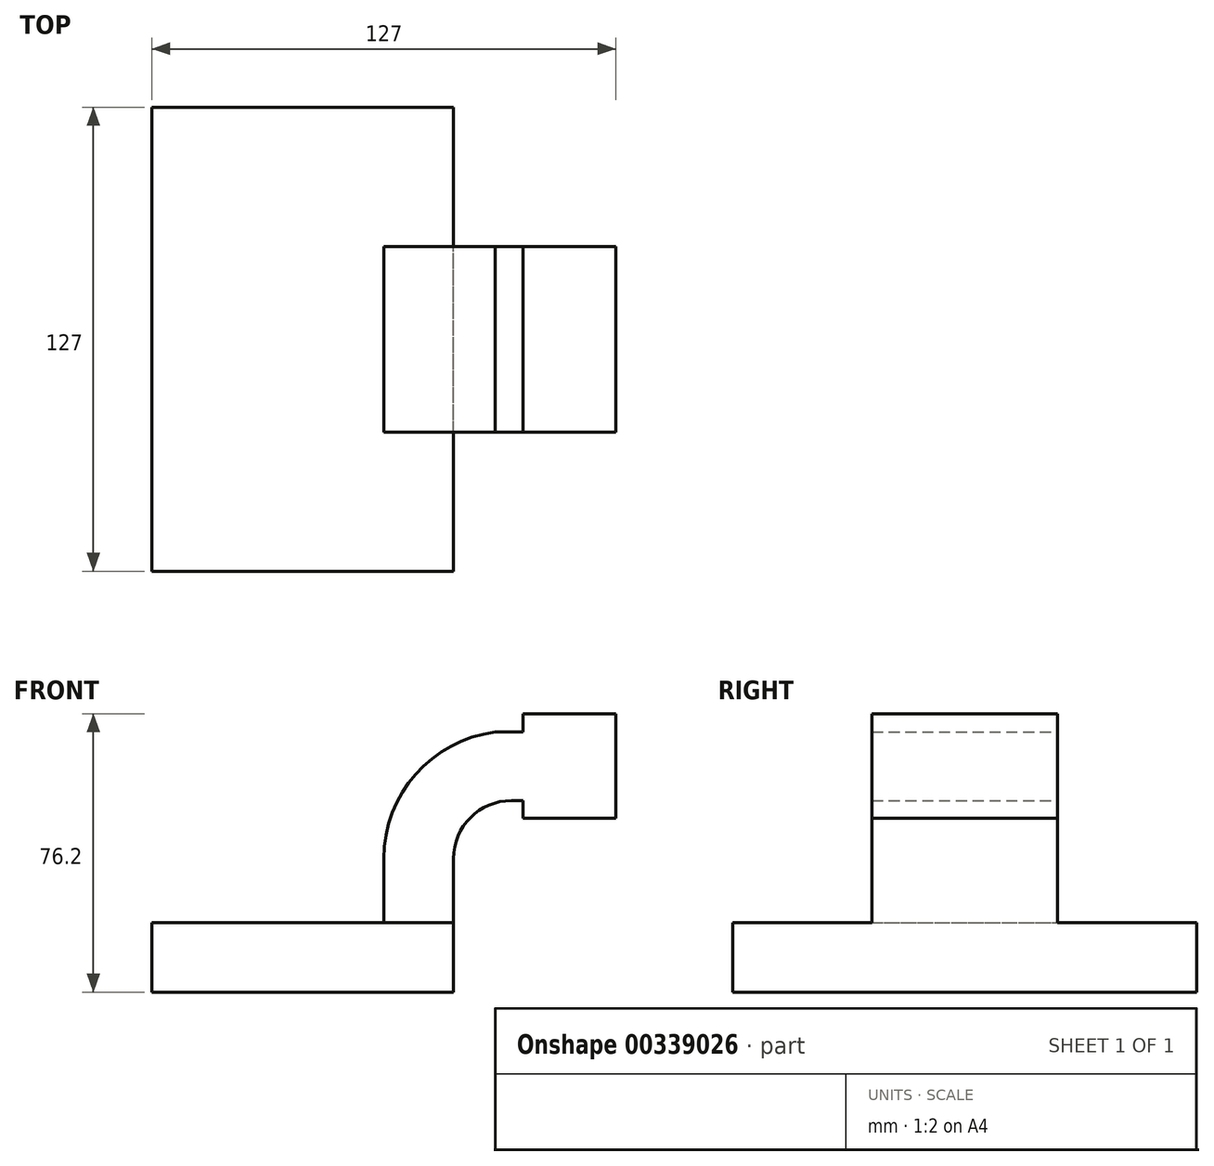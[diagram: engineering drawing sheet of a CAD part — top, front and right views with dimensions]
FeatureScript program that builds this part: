
annotation { "Feature Type Name" : "Feature", "Feature Type Description" : "" }
export const myFeature = defineFeature(function(context is Context, id is Id, definition is map)
    precondition{}
    {
        {
            var Q0;
            Q0=qCreatedBy(makeId("Front.planeOp"),FACE);
            var sketch = newSketch(context, id + "F0", { "sketchPlane" : qUnion([Q0])});
            skLineSegment(sketch, "E0.bottom", {"start": v(41.27, 9.53) * mm, "end": v(-41.27, 9.53) * mm});
            skLineSegment(sketch, "E0.top", {"start": v(41.28, -9.52) * mm, "end": v(-41.27, -9.53) * mm});
            skLineSegment(sketch, "E0.left", {"start": v(41.27, 9.53) * mm, "end": v(41.28, -9.52) * mm});
            skLineSegment(sketch, "E0.right", {"start": v(-41.27, 9.53) * mm, "end": v(-41.27, -9.52) * mm});
            skPoint(sketch, "E0.middle", {"position": v(0, 0) * mm});
            skLineSegment(sketch, "E1.bottom", {"start": v(60.32, 66.68) * mm, "end": v(111.12, 66.68) * mm});
            skLineSegment(sketch, "E1.top", {"start": v(60.32, 38.1) * mm, "end": v(111.12, 38.1) * mm});
            skLineSegment(sketch, "E1.left", {"start": v(60.32, 66.68) * mm, "end": v(60.32, 38.1) * mm});
            skLineSegment(sketch, "E1.right", {"start": v(111.12, 66.68) * mm, "end": v(111.12, 38.1) * mm});
            skPoint(sketch, "E1.middle", {"position": v(85.72, 52.39) * mm});
            skLineSegment(sketch, "E2", {"start": v(41.27, 9.53) * mm, "end": v(41.27, 27) * mm});
            skArc(sketch, "E3", {"start": v(41.27, 27) * mm, "mid": v(45.92, 38.23) * mm, "end": v(57.15, 42.88) * mm});
            skLineSegment(sketch, "E4", {"start": v(57.15, 42.88) * mm, "end": v(87.63, 42.88) * mm});
            skArc(sketch, "E5.1", {"start": v(22.22, 27) * mm, "mid": v(30.93, 50.07) * mm, "end": v(52.7, 61.64) * mm});
            skLineSegment(sketch, "E5.2", {"start": v(22.22, 9.53) * mm, "end": v(22.22, 27) * mm});
            skLineSegment(sketch, "E6", {"start": v(52.7, 61.64) * mm, "end": v(85.72, 61.64) * mm});
            skLineSegment(sketch, "E7", {"start": v(85.72, 38.1) * mm, "end": v(85.72, 66.67) * mm});
            skFitSpline(sketch, "E8", {"points": [v(-41.27, 9.52) * mm, v(52.7, 61.64) * mm], "startDerivative": vector(43.46, 113.8) * mm, "endDerivative": vector(127.96, -0.76) * mm});
            skSolve(sketch);
        }
        {
            var Q0;
            Q0=makeQuery(id+"F0.imprint","IMPRINT",FACE,{"disambiguationData":[TD([[makeQuery(id+"F0.imprint","IMPRINT",EDGE,{"derivedFrom":sQuery(id+"F0.wireOp",EDGE,"E0.top")}),-1.0]])]});
            extrude(context, id + "F1", {"entities" : qUnion([Q0]), "endBound" : BoundingType.SYMMETRIC, "depth" : 127 * mm});
        }
        {
            var Q0;
            {var subQ1=sQuery(id+"F0.wireOp",EDGE,"E2");Q0=makeQuery(id+"F0.imprint","IMPRINT",FACE,{"disambiguationData":[TD([[makeQuery(id+"F0.imprint","IMPRINT",EDGE,{"derivedFrom":subQ1}),1.0]])]});}
            var Q1;
            {var subQ6=sQuery(id+"F0.wireOp",EDGE,"E7");Q1=makeQuery(id+"F0.imprint","IMPRINT",FACE,{"disambiguationData":[TD([[makeQuery(id+"F0.imprint","IMPRINT",EDGE,{"derivedFrom":subQ6}),1.0]])]});}
            extrude(context, id + "F2", {"entities" : qUnion([Q0, Q1]), "operationType" : NewBodyOperationType.ADD, "endBound" : BoundingType.SYMMETRIC, "depth" : 50.8 * mm});
        }
        {
            var Q0;
            Q0=makeQuery(id+"F0.imprint","IMPRINT",FACE,{"disambiguationData":[TD([[makeQuery(id+"F0.imprint","IMPRINT",EDGE,{"derivedFrom":sQuery(id+"F0.wireOp",EDGE,"E5.1")}),1.0]])]});
            extrude(context, id + "F3", {"entities" : qUnion([Q0]), "operationType" : NewBodyOperationType.ADD, "endBound" : BoundingType.SYMMETRIC, "depth" : 15.88 * mm});
        }
    });
